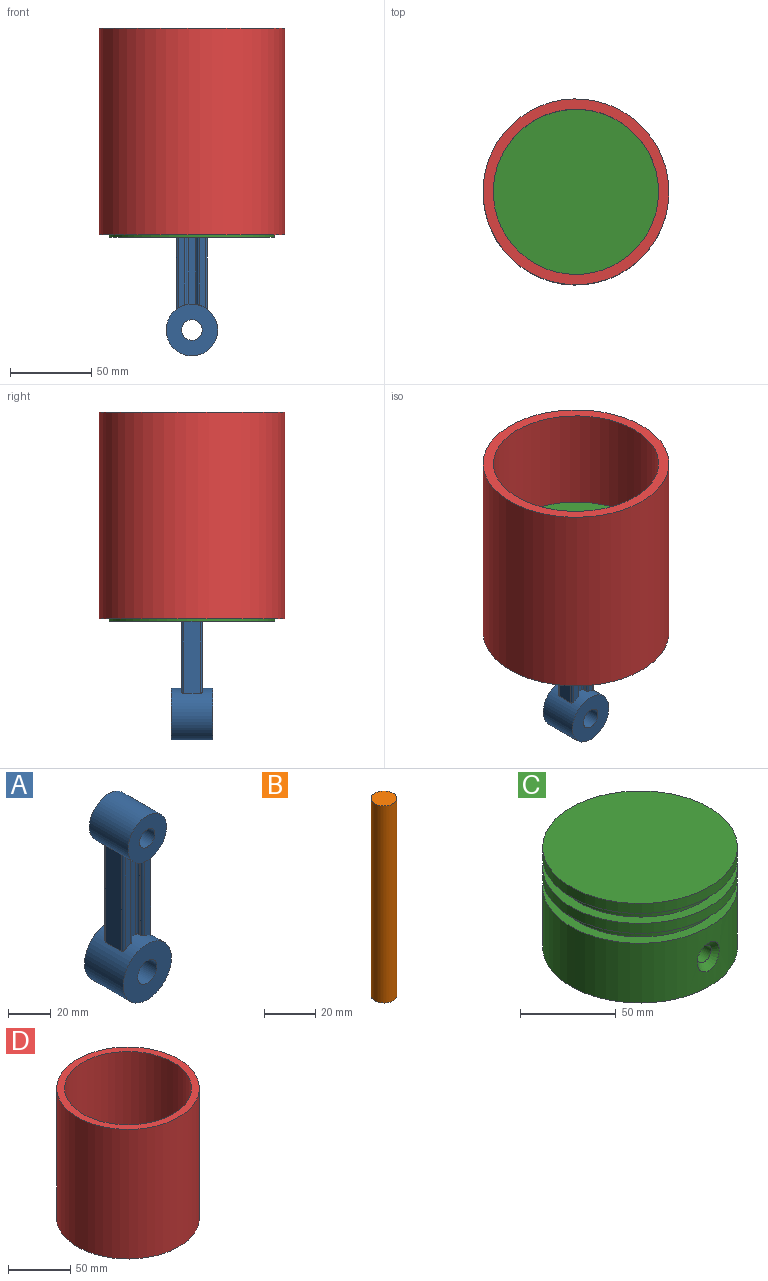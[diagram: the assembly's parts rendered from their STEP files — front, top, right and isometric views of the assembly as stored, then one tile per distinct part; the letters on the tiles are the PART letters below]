
ASSEMBLY  parts=4 mates=3
PART A: 32 faces, bbox 31.8x25.4x104.8 mm
  f0: cylinder r=1.27mm len=55.1mm, axis (0,0,-1), area 108.3mm2, adj f1,f23,f24,f29
  f1: plane 55.1x10.16mm, normal (-1,0,0), area 559.8mm2, adj f0,f2,f24,f29
  f2: cylinder r=1.27mm len=55.1mm, axis (0,0,-1), area 108.3mm2, adj f1,f18,f24,f29
  f3: cylinder r=1.27mm len=49.06mm, axis (0,0,-1), area 96.9mm2, adj f4,f18,f24,f29
  f4: plane 48.35x0.64mm, normal (1,0,0), area 30.7mm2, adj f3,f5,f24,f29
  f5: cylinder r=1.27mm len=48.35mm, axis (0,0,-1), area 96mm2, adj f4,f19,f24,f29
  f6: cylinder r=1.27mm len=48.35mm, axis (0,0,-1), area 96mm2, adj f7,f19,f24,f29
  f7: plane 48.35x0.64mm, normal (-1,0,0), area 30.7mm2, adj f6,f8,f24,f29
  f8: cylinder r=1.27mm len=49.06mm, axis (0,0,-1), area 96.9mm2, adj f7,f20,f24,f29
  f9: cylinder r=1.27mm len=55.1mm, axis (0,0,-1), area 108.3mm2, adj f10,f20,f24,f29
  f10: plane 55.1x10.16mm, normal (1,0,0), area 559.8mm2, adj f9,f11,f24,f29
  f11: cylinder r=1.27mm len=55.1mm, axis (0,0,-1), area 108.3mm2, adj f10,f21,f24,f29
  f12: cylinder r=1.27mm len=49.06mm, axis (0,0,-1), area 96.9mm2, adj f13,f21,f24,f29
  f13: plane 48.35x0.64mm, normal (-1,0,0), area 30.7mm2, adj f12,f14,f24,f29
  f14: cylinder r=1.27mm len=48.35mm, axis (0,0,-1), area 96mm2, adj f13,f22,f24,f29
  f15: cylinder r=1.27mm len=48.35mm, axis (0,0,-1), area 96mm2, adj f16,f22,f24,f29
  f16: plane 48.35x0.64mm, normal (1,0,0), area 30.7mm2, adj f15,f17,f24,f29
  f17: cylinder r=1.27mm len=49.06mm, axis (0,0,-1), area 96.9mm2, adj f16,f23,f24,f29
  f18: plane 52.99x3.81mm, normal (0,-1,0), area 193.5mm2, adj f2,f3,f24,f29
  f19: plane 47.88x3.81mm, normal (0,-1,0), area 181.8mm2, adj f5,f6,f24,f29
  f20: plane 52.99x3.81mm, normal (0,-1,0), area 193.5mm2, adj f8,f9,f24,f29
  f21: plane 52.99x3.81mm, normal (0,1,0), area 193.5mm2, adj f11,f12,f24,f29
  f22: plane 47.88x3.81mm, normal (0,1,0), area 181.8mm2, adj f14,f15,f24,f29
  f23: plane 52.99x3.81mm, normal (0,1,0), area 193.5mm2, adj f0,f17,f24,f29
  f24: cylinder r=12.7mm len=25.4mm, axis (0,1,0), area 1796.1mm2, adj f0,f1,f2,f3,f4,f5,f6,f7
  f25: plane 25.4x25.4mm, normal (0,-1,0), area 425.6mm2, adj f24,f27
  f26: plane 25.4x25.4mm, normal (0,1,0), area 425.6mm2, adj f24,f27
  f27: cylinder r=5.08mm len=25.4mm, axis (0,-1,0), area 810.7mm2, adj f25,f26
  f28: cylinder r=6.35mm len=25.4mm, axis (0,-1,0), area 1013.4mm2, adj f30,f31
  f29: cylinder r=15.88mm len=31.75mm, axis (0,-1,0), area 2316.4mm2, adj f0,f1,f2,f3,f4,f5,f6,f7
  f30: plane 31.75x31.75mm, normal (0,1,0), area 665.1mm2, adj f28,f29
  f31: plane 31.75x31.75mm, normal (0,-1,0), area 665.1mm2, adj f28,f29
PART B: 3 faces, bbox 10.2x10.2x94.6 mm
  f0: cylinder r=5.08mm len=94.62mm, axis (0,0,-1), area 3020.1mm2, adj f1,f2
  f1: plane 10.16x10.16mm, normal (0,0,1), area 81.1mm2, adj f0
  f2: plane 10.16x10.16mm, normal (0,0,-1), area 81.1mm2, adj f0
PART C: 33 faces, bbox 101.7x101.7x63.6 mm
  f0: plane 85.2x31.76mm, normal (-1,0,0), area 1950.6mm2, adj f1,f5,f6,f7,f8,f9,f10,f26
  f1: cylinder r=12.7mm len=31.83mm, axis (0,1,0), area 1233.2mm2, adj f0,f10,f25,f30
  f2: cylinder r=5.08mm len=34.71mm, axis (0,1,0), area 1107.3mm2, adj f27,f30
  f3: plane 101.6x101.6mm, normal (0,0,1), area 8107.3mm2, adj f19
  f4: cylinder r=50.8mm len=101.6mm, axis (0,0,1), area 11702.9mm2, adj f11,f12,f27,f29
  f5: plane 58.2x19.05mm, normal (0,0,-1), area 799.1mm2, adj f0,f6
  f6: torus R=31.75mm, axis (0,0,1), area 862.5mm2, adj f0,f5,f7
  f7: cylinder r=38.1mm len=71.84mm, axis (0,0,1), area 893.4mm2, adj f0,f6,f8
  f8: torus R=41.27mm, axis (0,0,1), area 486mm2, adj f0,f7,f9
  f9: torus R=41.27mm, axis (0,0,1), area 549.8mm2, adj f0,f8,f10
  f10: cylinder r=44.45mm len=88.9mm, axis (0,0,1), area 6977.9mm2, adj f0,f1,f9,f11,f24,f25,f26
  f11: plane 101.6x101.6mm, normal (0,0,-1), area 1900.2mm2, adj f4,f10
  f12: plane 101.6x101.6mm, normal (0,0,1), area 1721.5mm2, adj f4,f13
  f13: cylinder r=45.09mm len=90.17mm, axis (0,0,1), area 1798.8mm2, adj f12,f14
  f14: plane 101.6x101.6mm, normal (0,0,-1), area 1721.5mm2, adj f13,f15
  f15: cylinder r=50.8mm len=101.6mm, axis (0,0,1), area 2026.8mm2, adj f14,f16
  f16: plane 101.6x101.6mm, normal (0,0,1), area 1721.5mm2, adj f15,f17
  f17: cylinder r=45.09mm len=90.17mm, axis (0,0,1), area 1798.8mm2, adj f16,f18
  f18: plane 101.6x101.6mm, normal (0,0,-1), area 1721.5mm2, adj f17,f19
  f19: cylinder r=50.8mm len=101.6mm, axis (0,0,1), area 2026.8mm2, adj f3,f18
  f20: plane 58.2x19.05mm, normal (0,0,-1), area 799.1mm2, adj f21,f25
  f21: torus R=31.75mm, axis (0,0,1), area 862.5mm2, adj f20,f22,f25
  f22: cylinder r=38.1mm len=71.84mm, axis (0,0,1), area 893.4mm2, adj f21,f23,f25
  f23: torus R=41.27mm, axis (0,0,1), area 486mm2, adj f22,f24,f25
  f24: torus R=41.27mm, axis (0,0,1), area 549.8mm2, adj f10,f23,f25
  f25: plane 85.2x31.76mm, normal (1,0,0), area 1950.6mm2, adj f1,f10,f20,f21,f22,f23,f24,f26
  f26: cylinder r=12.7mm len=31.75mm, axis (0,1,0), area 1230mm2, adj f0,f10,f25,f31
  f27: cone r=5.08mm half-angle=47.5deg, axis (0,1,0), area 199.3mm2, adj f2,f4
  f28: cylinder r=5.08mm len=34.61mm, axis (0,1,0), area 1104.7mm2, adj f29,f31
  f29: cone r=5.08mm half-angle=47.5deg, axis (0,-1,0), area 199.3mm2, adj f4,f28
  f30: plane 31.91x25.51mm, normal (0,-1,0), area 657.5mm2, adj f0,f1,f2,f25,f32
  f31: plane 31.7x25.4mm, normal (0,1,0), area 654.8mm2, adj f0,f25,f26,f28,f32
  f32: plane 25.4x25.24mm, normal (0,0,-1), area 641mm2, adj f0,f25,f30,f31
PART D: 4 faces, bbox 114.3x114.3x127 mm
  f0: cylinder r=50.8mm len=127mm, axis (0,0,-1), area 40536.6mm2, adj f2,f3
  f1: cylinder r=57.15mm len=127mm, axis (0,0,-1), area 45603.7mm2, adj f2,f3
  f2: plane 114.3x114.3mm, normal (0,0,1), area 2153.5mm2, adj f0,f1
  f3: plane 114.3x114.3mm, normal (0,0,-1), area 2153.5mm2, adj f0,f1
PLACE A t=(25.93,-102.82,-24.22)mm
PLACE B rot(axis=(-1,0,0),90deg) t=(82.14,-146.95,48.67)mm
PLACE C t=(-85.15,-99.64,32.93)mm
PLACE D t=(-235.49,-99.64,34.36)mm fixed
MATE revolute A.f27 <-> B.f0  axis (0,1,0) through (-85.15,-99.64,51.98)mm
MATE fastened B.f0 <-> C.f2  axis (0,-1,0) through (-85.15,-146.95,51.98)mm
MATE slider D.f0 <-> C.f4  axis (0,0,-1) through (-85.15,-99.64,34.36)mm
